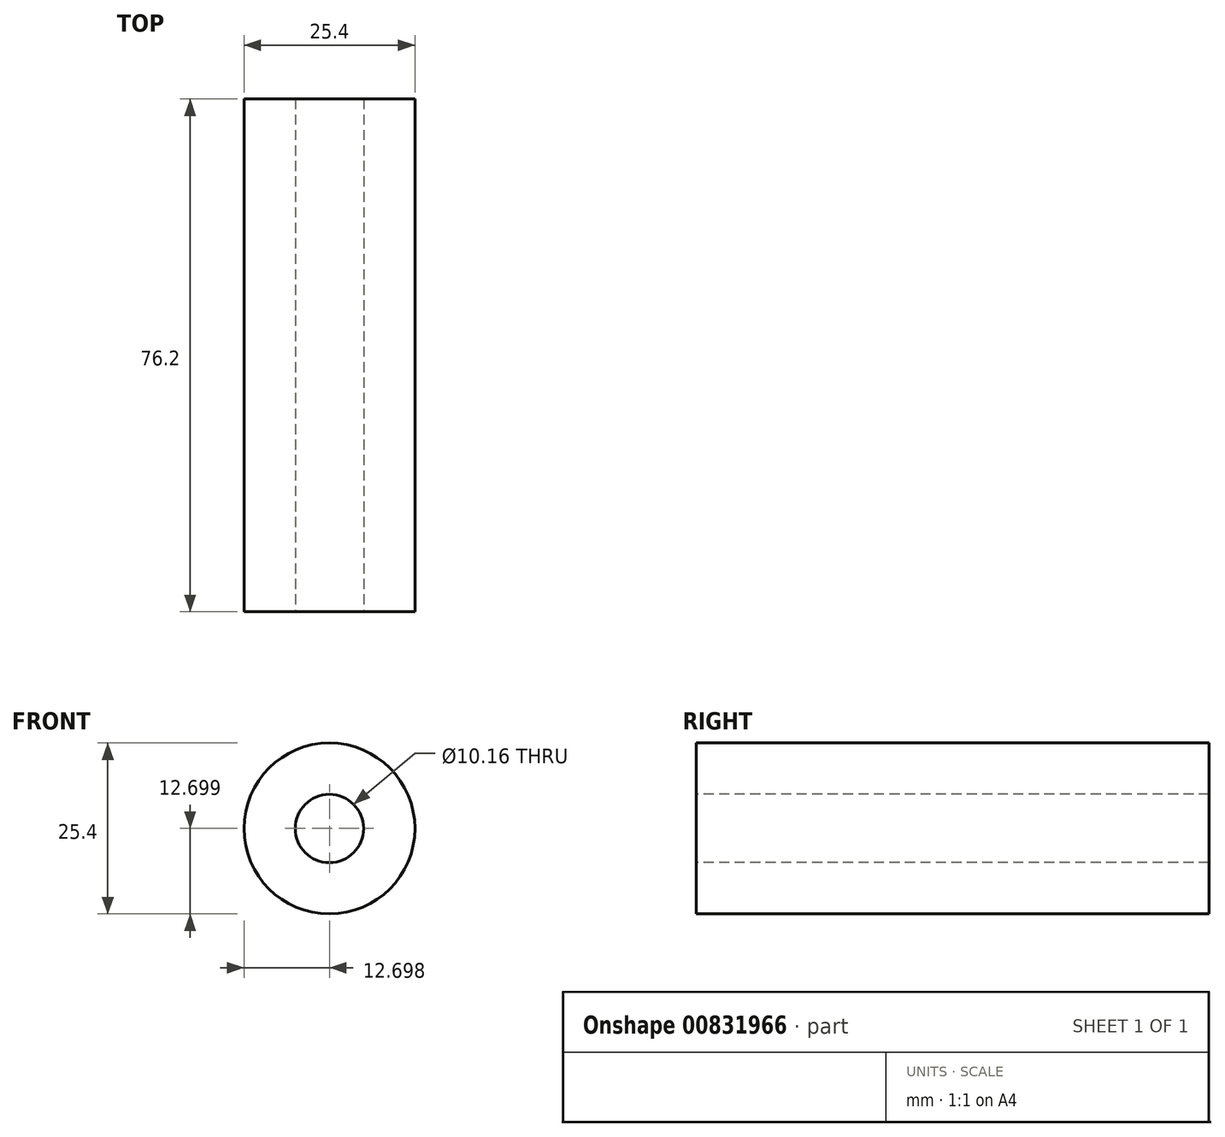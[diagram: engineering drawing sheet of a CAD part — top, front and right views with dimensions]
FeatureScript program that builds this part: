
annotation { "Feature Type Name" : "Feature", "Feature Type Description" : "" }
export const myFeature = defineFeature(function(context is Context, id is Id, definition is map)
    precondition{}
    {
        {
            var Q0;
            Q0=qCreatedBy(makeId("Front.planeOp"),FACE);
            var sketch = newSketch(context, id + "F0", { "sketchPlane" : qUnion([Q0])});
            skCircle(sketch, "E0", {"center": v(-41.5, 18.88) * mm, "radius": 12.7 * mm});
            skCircle(sketch, "E1", {"center": v(-41.5, 18.88) * mm, "radius": 5.08 * mm});
            skSolve(sketch);
        }
        {
            var Q0;
            Q0 = qSketchRegion(id + "F0", true);
            extrude(context, id + "F1", {"entities" : qUnion([Q0]), "oppositeDirection" : true, "depth" : 76.2 * mm, "offsetDistance" : 25.4 * mm});
        }
    });
